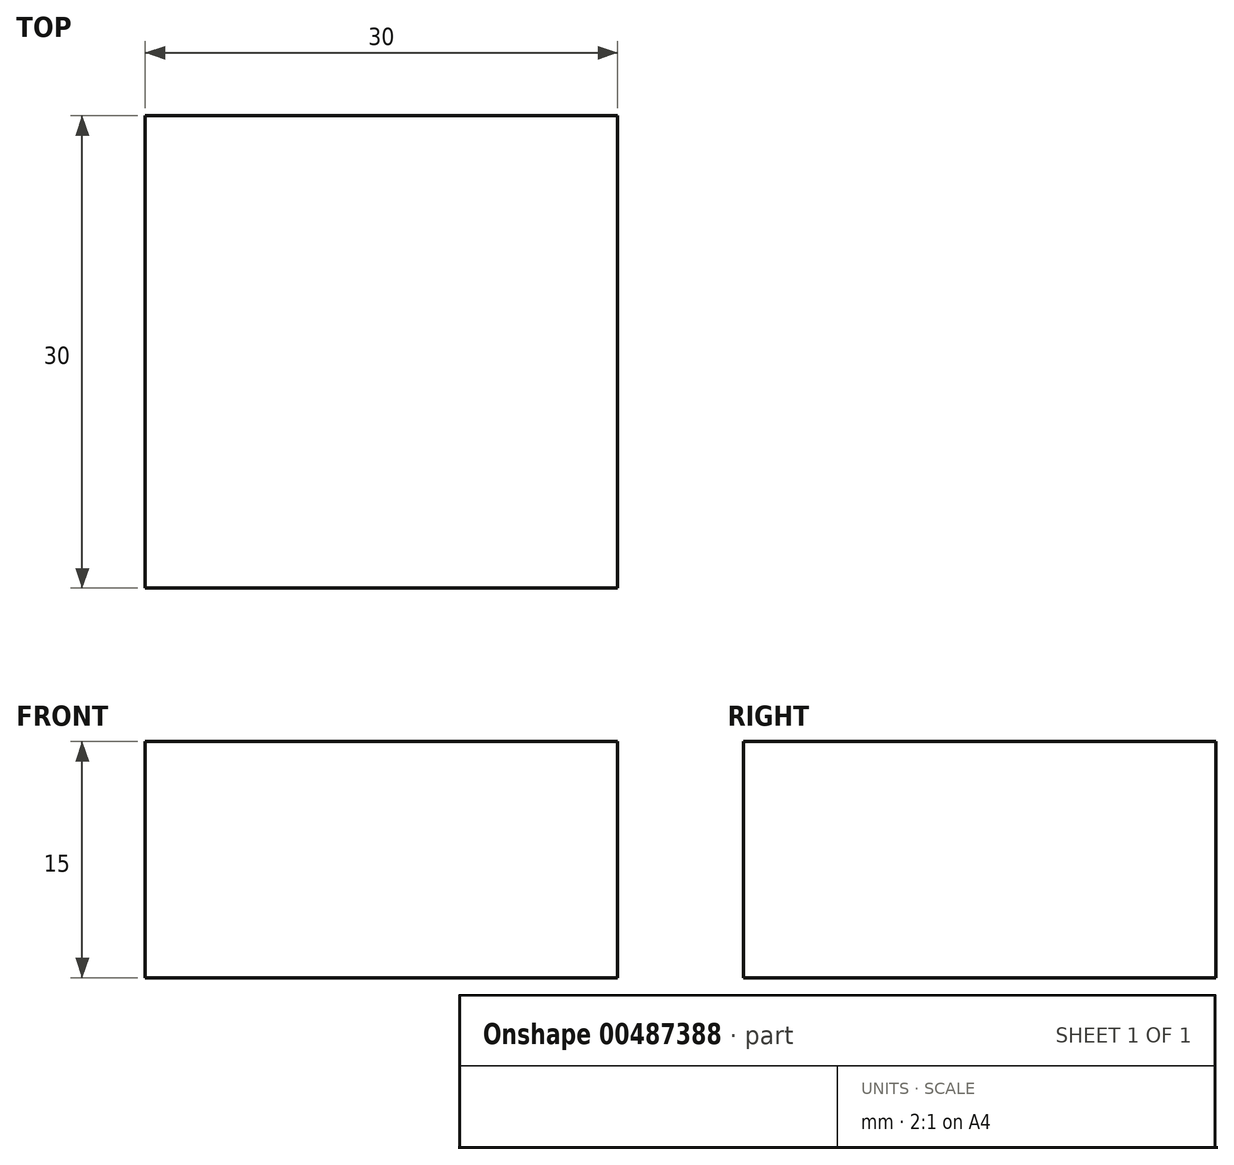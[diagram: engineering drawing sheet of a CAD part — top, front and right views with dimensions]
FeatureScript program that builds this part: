
annotation { "Feature Type Name" : "Feature", "Feature Type Description" : "" }
export const myFeature = defineFeature(function(context is Context, id is Id, definition is map)
    precondition{}
    {
        {
            var Q0;
            Q0=qCreatedBy(makeId("Top.planeOp"),FACE);
            var sketch = newSketch(context, id + "F0", { "sketchPlane" : qUnion([Q0])});
            skLineSegment(sketch, "E0.bottom", {"start": v(-30, 76.82) * mm, "end": v(0, 76.82) * mm});
            skLineSegment(sketch, "E0.top", {"start": v(-30, 46.82) * mm, "end": v(0, 46.82) * mm});
            skLineSegment(sketch, "E0.left", {"start": v(-30, 76.82) * mm, "end": v(-30, 46.82) * mm});
            skLineSegment(sketch, "E0.right", {"start": v(0, 76.82) * mm, "end": v(0, 46.82) * mm});
            skSolve(sketch);
        }
        {
            var Q0;
            Q0=makeQuery(id+"F0.imprint","IMPRINT",FACE,{"disambiguationData":[TD([[makeQuery(id+"F0.imprint","IMPRINT",EDGE,{"derivedFrom":sQuery(id+"F0.wireOp",EDGE,"E0.bottom")}),-1.0]])]});
            extrude(context, id + "F1", {"entities" : qUnion([Q0]), "depth" : 15 * mm});
        }
    });
